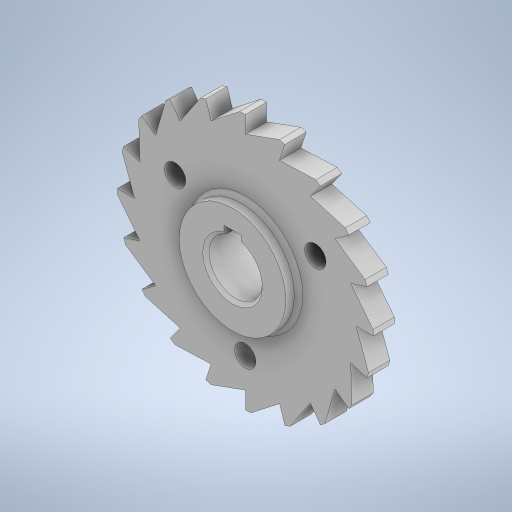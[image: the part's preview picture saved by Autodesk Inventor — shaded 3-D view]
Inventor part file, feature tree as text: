
AUTODESK INVENTOR PART (.ipt)
format: ipt  version: 2023 (Build 270158000, 158)  size: 402,432 bytes
history: native  units: mm
features: extrude x2, sketch x1, fillet x1, chamfer x1
ambient origin geometry x8: Origin, YZ Plane, XZ Plane, XY Plane, X Axis, Y Axis, Z Axis, Center Point
bodies: Solid1 (feature_tree)
feature tree (5):
  sketch  "Sketch1"  dims[d0=25.0mm d1=8.0mm d2=28.5mm d3=50.0mm d4=76.0mm d5=120.0mm d6=10.0mm d7=60.0deg d8=30.0mm d10=360.0deg d12=8.0mm d13=12.217305mm d14=8.0mm d15=3.141593mm d17=200.0mm d19=360.0deg d21=17.033165mm d22=22.0mm d23=0.0mm d24=10.0mm d25=0.0mm d26=2.0mm d27=1.5mm d28=2.0mm d29=45.0deg]
  extrude  "Extrusion1"  Depth=8.0mm
  extrude  "Extrusion2"  Depth=10.0mm
  fillet  "Fillet1"  Radius=50.0mm
  chamfer  "Chamfer1"  Distance=76.0mm
